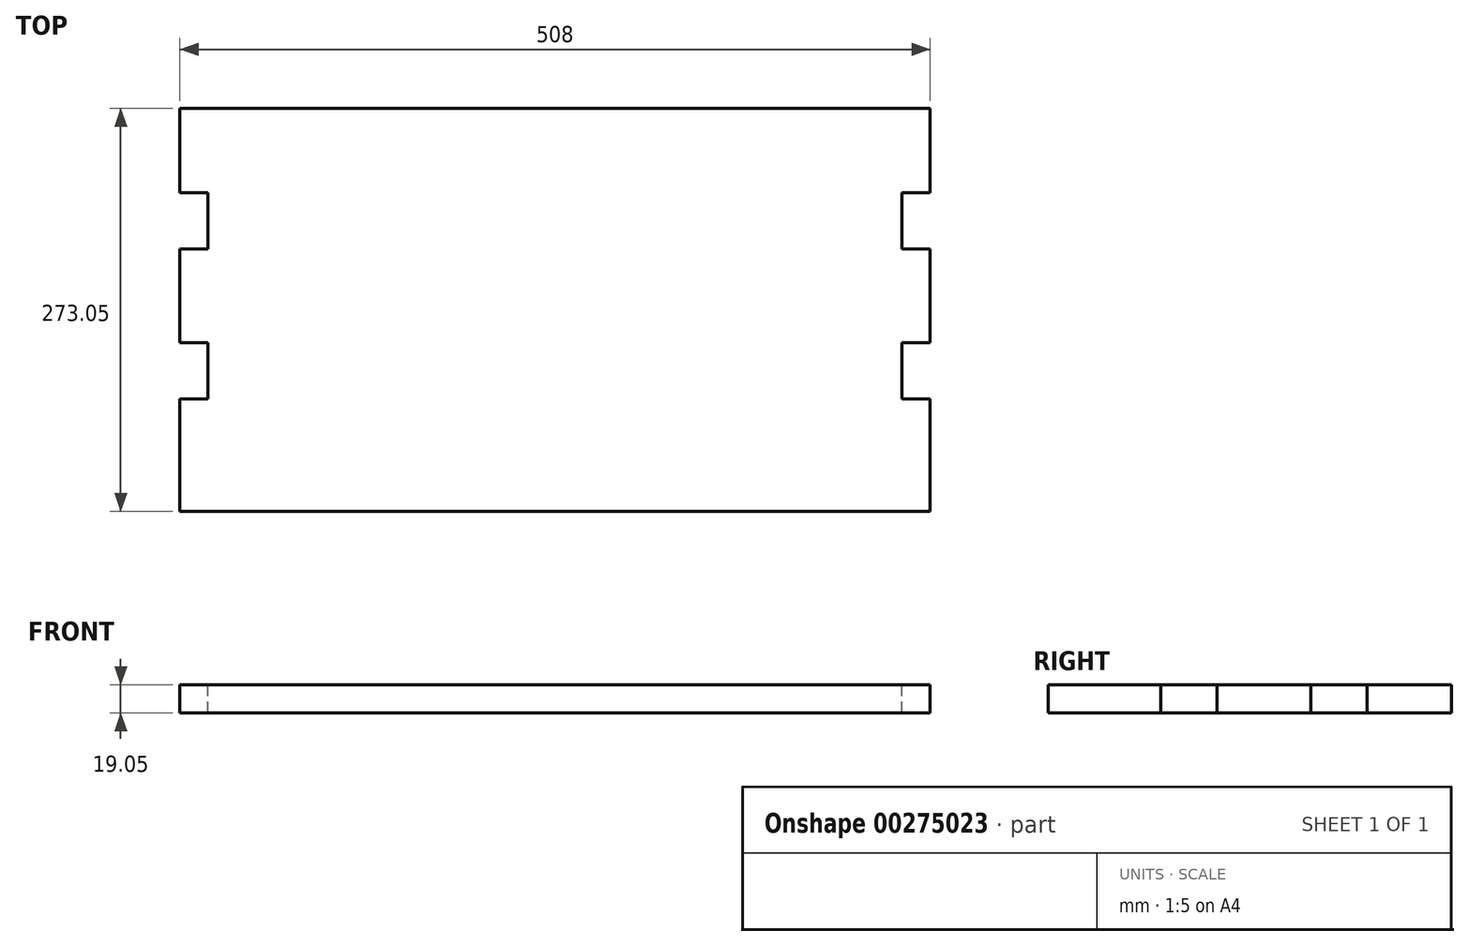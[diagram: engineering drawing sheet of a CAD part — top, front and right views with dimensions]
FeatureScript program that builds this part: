
annotation { "Feature Type Name" : "Feature", "Feature Type Description" : "" }
export const myFeature = defineFeature(function(context is Context, id is Id, definition is map)
    precondition{}
    {
        {
            var Q0;
            Q0=qCreatedBy(makeId("Top.planeOp"),FACE);
            var sketch = newSketch(context, id + "F0", { "sketchPlane" : qUnion([Q0])});
            skLineSegment(sketch, "E0.bottom", {"start": v(-273.6, 195.68) * mm, "end": v(234.4, 195.68) * mm});
            skLineSegment(sketch, "E0.top", {"start": v(-273.6, -58.32) * mm, "end": v(234.4, -58.32) * mm});
            skLineSegment(sketch, "E0.left", {"start": v(-273.6, 195.68) * mm, "end": v(-273.6, -58.32) * mm});
            skLineSegment(sketch, "E0.right", {"start": v(234.4, 195.68) * mm, "end": v(234.4, -58.32) * mm});
            skSolve(sketch);
        }
        {
            var Q0;
            Q0 = qSketchRegion(id + "F0", true);
            extrude(context, id + "F1", {"entities" : qUnion([Q0]), "depth" : 19.05 * mm});
        }
        {
            var Q0;
            Q0=makeQuery(id+"F1.opExtrude","CAP_FACE",FACE,{"disambiguationData":[OSD([sQuery(id+"F0.wireOp",EDGE,"E0.bottom"),sQuery(id+"F0.wireOp",EDGE,"E0.top"),sQuery(id+"F0.wireOp",EDGE,"E0.left"),sQuery(id+"F0.wireOp",EDGE,"E0.right")])],"isStart":false});
            var sketch = newSketch(context, id + "F2", { "sketchPlane" : qUnion([Q0])});
            skLineSegment(sketch, "E1.bottom", {"start": v(-273.6, 138.53) * mm, "end": v(-254.55, 138.53) * mm});
            skLineSegment(sketch, "E1.top", {"start": v(-273.6, 100.43) * mm, "end": v(-254.55, 100.43) * mm});
            skLineSegment(sketch, "E1.left", {"start": v(-273.6, 138.53) * mm, "end": v(-273.6, 100.43) * mm});
            skLineSegment(sketch, "E1.right", {"start": v(-254.55, 138.53) * mm, "end": v(-254.55, 100.43) * mm});
            skLineSegment(sketch, "E2.bottom", {"start": v(-273.6, 36.93) * mm, "end": v(-254.55, 36.93) * mm});
            skLineSegment(sketch, "E2.top", {"start": v(-273.6, -1.17) * mm, "end": v(-254.55, -1.17) * mm});
            skLineSegment(sketch, "E2.left", {"start": v(-273.6, 36.93) * mm, "end": v(-273.6, -1.17) * mm});
            skLineSegment(sketch, "E2.right", {"start": v(-254.55, 36.93) * mm, "end": v(-254.55, -1.17) * mm});
            skLineSegment(sketch, "E3.bottom", {"start": v(234.4, 138.53) * mm, "end": v(215.35, 138.53) * mm});
            skLineSegment(sketch, "E3.top", {"start": v(234.4, 100.43) * mm, "end": v(215.35, 100.43) * mm});
            skLineSegment(sketch, "E3.left", {"start": v(234.4, 138.53) * mm, "end": v(234.4, 100.43) * mm});
            skLineSegment(sketch, "E3.right", {"start": v(215.35, 138.53) * mm, "end": v(215.35, 100.43) * mm});
            skLineSegment(sketch, "E4.bottom", {"start": v(234.4, 36.93) * mm, "end": v(215.35, 36.93) * mm});
            skLineSegment(sketch, "E4.top", {"start": v(234.4, -1.17) * mm, "end": v(215.35, -1.17) * mm});
            skLineSegment(sketch, "E4.left", {"start": v(234.4, 36.93) * mm, "end": v(234.4, -1.17) * mm});
            skLineSegment(sketch, "E4.right", {"start": v(215.35, 36.93) * mm, "end": v(215.35, -1.17) * mm});
            skSolve(sketch);
        }
        {
            var Q0;
            Q0 = qSketchRegion(id + "F2", true);
            extrude(context, id + "F3", {"entities" : qUnion([Q0]), "operationType" : NewBodyOperationType.REMOVE, "oppositeDirection" : true, "depth" : 19.05 * mm});
        }
        {
            var Q0;
            Q0=makeQuery(id+"F1.opExtrude","SWEPT_FACE",FACE,{"disambiguationData":[OSD([sQuery(id+"F0.wireOp",EDGE,"E0.top")])]});
            var sketch = newSketch(context, id + "F4", { "sketchPlane" : qUnion([Q0])});
            skLineSegment(sketch, "E5.bottom", {"start": v(-273.6, 19.05) * mm, "end": v(234.4, 19.05) * mm});
            skLineSegment(sketch, "E5.top", {"start": v(-273.6, 0) * mm, "end": v(234.4, 0) * mm});
            skLineSegment(sketch, "E5.left", {"start": v(-273.6, 19.05) * mm, "end": v(-273.6, 0) * mm});
            skLineSegment(sketch, "E5.right", {"start": v(234.4, 19.05) * mm, "end": v(234.4, 0) * mm});
            skSolve(sketch);
        }
        {
            var Q0;
            Q0 = qSketchRegion(id + "F4", true);
            extrude(context, id + "F5", {"entities" : qUnion([Q0]), "operationType" : NewBodyOperationType.ADD, "depth" : 19.05 * mm});
        }
    });
